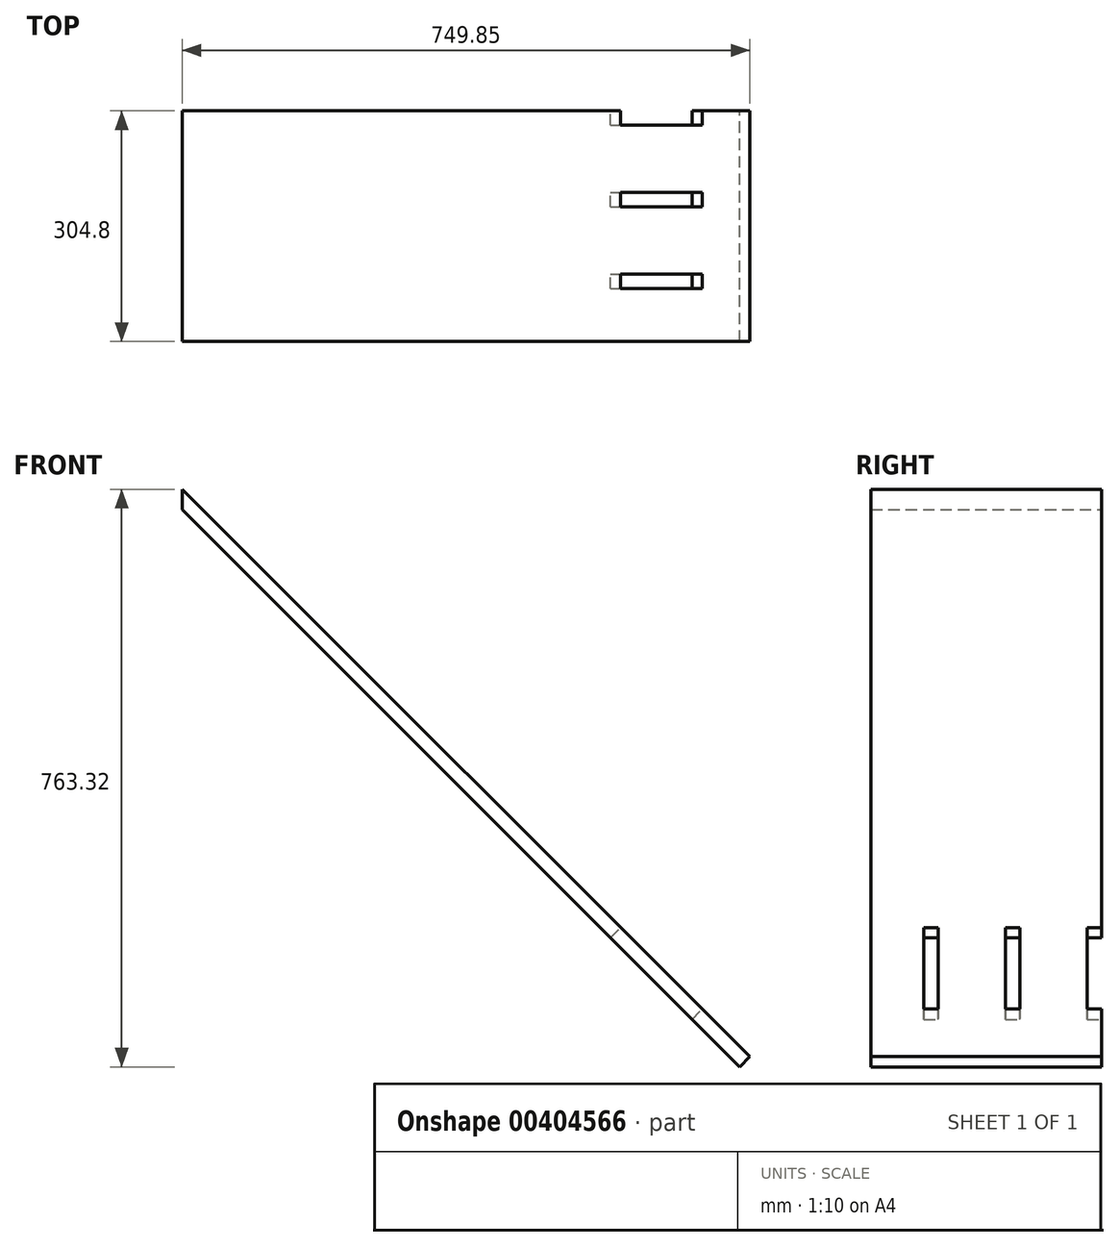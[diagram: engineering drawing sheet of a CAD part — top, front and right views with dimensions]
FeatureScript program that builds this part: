
annotation { "Feature Type Name" : "Feature", "Feature Type Description" : "" }
export const myFeature = defineFeature(function(context is Context, id is Id, definition is map)
    precondition{}
    {
        {
            var Q0;
            Q0=qCreatedBy(makeId("Front.planeOp"),FACE);
            var sketch = newSketch(context, id + "F0", { "sketchPlane" : qUnion([Q0])});
            skLineSegment(sketch, "E0.right", {"start": v(-341.41, 790.1) * mm, "end": v(-341.41, 817.04) * mm});
            skLineSegment(sketch, "E1.MirrorCS", {"start": v(394.97, 53.72) * mm, "end": v(-341.41, 790.1) * mm});
            skLineSegment(sketch, "E2.MirrorCS", {"start": v(408.44, 67.2) * mm, "end": v(-341.41, 817.04) * mm});
            skLineSegment(sketch, "E3", {"start": v(408.44, 67.2) * mm, "end": v(394.97, 53.72) * mm});
            skSolve(sketch);
        }
        {
            var Q0;
            Q0=qSketchRegion(id+"F0",true);
            extrude(context, id + "F1", {"entities" : qUnion([Q0]), "endBound" : BoundingType.SYMMETRIC, "depth" : 304.8 * mm});
        }
        {
            var Q0;
            Q0=makeQuery(id+"F1.opExtrude","SWEPT_FACE",FACE,{"disambiguationData":[OSD([sQuery(id+"F0.wireOp",EDGE,"E2.MirrorCS")])]});
            var sketch = newSketch(context, id + "F2", { "sketchPlane" : qUnion([Q0])});
            skLineSegment(sketch, "E4.bottom", {"start": v(-711.2, -152.4) * mm, "end": v(-730.25, -152.4) * mm});
            skLineSegment(sketch, "E4.top", {"start": v(-711.2, 0) * mm, "end": v(-730.25, 0) * mm});
            skLineSegment(sketch, "E4.left", {"start": v(-730.25, 0) * mm, "end": v(-730.25, -152.4) * mm});
            skLineSegment(sketch, "E4.right", {"start": v(-711.2, 0) * mm, "end": v(-711.2, -152.4) * mm});
            skLineSegment(sketch, "E5.bottom", {"start": v(-622.3, -152.4) * mm, "end": v(-603.25, -152.4) * mm});
            skLineSegment(sketch, "E5.top", {"start": v(-622.3, 0) * mm, "end": v(-603.25, 0) * mm});
            skLineSegment(sketch, "E5.left", {"start": v(-622.3, 0) * mm, "end": v(-622.3, -152.4) * mm});
            skLineSegment(sketch, "E5.right", {"start": v(-603.25, 0) * mm, "end": v(-603.25, -152.4) * mm});
            skLineSegment(sketch, "E6.bottom", {"start": v(-514.35, -152.4) * mm, "end": v(-495.3, -152.4) * mm});
            skLineSegment(sketch, "E6.top", {"start": v(-514.35, 0) * mm, "end": v(-495.3, 0) * mm});
            skLineSegment(sketch, "E6.left", {"start": v(-514.35, 0) * mm, "end": v(-514.35, -152.4) * mm});
            skLineSegment(sketch, "E6.right", {"start": v(-495.3, 0) * mm, "end": v(-495.3, -152.4) * mm});
            skLineSegment(sketch, "E7.bottom", {"start": v(-406.4, -152.4) * mm, "end": v(-387.35, -152.4) * mm});
            skLineSegment(sketch, "E7.top", {"start": v(-406.4, 0) * mm, "end": v(-387.35, 0) * mm});
            skLineSegment(sketch, "E7.left", {"start": v(-406.4, 0) * mm, "end": v(-406.4, -152.4) * mm});
            skLineSegment(sketch, "E7.right", {"start": v(-387.35, 0) * mm, "end": v(-387.35, -152.4) * mm});
            skLineSegment(sketch, "E8.bottom", {"start": v(-298.45, -152.4) * mm, "end": v(-279.4, -152.4) * mm});
            skLineSegment(sketch, "E8.top", {"start": v(-298.45, 0) * mm, "end": v(-279.4, 0) * mm});
            skLineSegment(sketch, "E8.left", {"start": v(-298.45, 0) * mm, "end": v(-298.45, -152.4) * mm});
            skLineSegment(sketch, "E8.right", {"start": v(-279.4, 0) * mm, "end": v(-279.4, -152.4) * mm});
            skLineSegment(sketch, "E9.bottom", {"start": v(-190.5, -152.4) * mm, "end": v(-171.45, -152.4) * mm});
            skLineSegment(sketch, "E9.top", {"start": v(-190.5, 0) * mm, "end": v(-171.45, 0) * mm});
            skLineSegment(sketch, "E9.left", {"start": v(-190.5, 0) * mm, "end": v(-190.5, -152.4) * mm});
            skLineSegment(sketch, "E9.right", {"start": v(-171.45, 0) * mm, "end": v(-171.45, -152.4) * mm});
            skLineSegment(sketch, "E10.bottom", {"start": v(-82.55, -152.4) * mm, "end": v(-63.5, -152.4) * mm});
            skLineSegment(sketch, "E10.top", {"start": v(-82.55, 0) * mm, "end": v(-63.5, 0) * mm});
            skLineSegment(sketch, "E10.left", {"start": v(-82.55, 0) * mm, "end": v(-82.55, -152.4) * mm});
            skLineSegment(sketch, "E10.right", {"start": v(-63.5, 0) * mm, "end": v(-63.5, -152.4) * mm});
            skLineSegment(sketch, "E11.bottom", {"start": v(25.4, -152.4) * mm, "end": v(44.45, -152.4) * mm});
            skLineSegment(sketch, "E11.top", {"start": v(25.4, 0) * mm, "end": v(44.45, 0) * mm});
            skLineSegment(sketch, "E11.left", {"start": v(25.4, 0) * mm, "end": v(25.4, -152.4) * mm});
            skLineSegment(sketch, "E11.right", {"start": v(44.45, 0) * mm, "end": v(44.45, -152.4) * mm});
            skLineSegment(sketch, "E12.bottom", {"start": v(133.35, -152.4) * mm, "end": v(152.4, -152.4) * mm});
            skLineSegment(sketch, "E12.top", {"start": v(133.35, 0) * mm, "end": v(152.4, 0) * mm});
            skLineSegment(sketch, "E12.left", {"start": v(133.35, 0) * mm, "end": v(133.35, -152.4) * mm});
            skLineSegment(sketch, "E12.right", {"start": v(152.4, 0) * mm, "end": v(152.4, -152.4) * mm});
            skSolve(sketch);
        }
        {
            var Q0;
            Q0=qSketchRegion(id+"F2",true);
            extrude(context, id + "F3", {"entities" : qUnion([Q0]), "operationType" : NewBodyOperationType.REMOVE, "oppositeDirection" : true, "depth" : 19.05 * mm});
        }
    });
